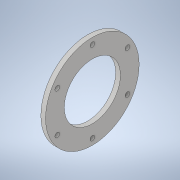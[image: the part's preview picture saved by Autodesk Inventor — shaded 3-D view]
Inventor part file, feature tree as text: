
AUTODESK INVENTOR PART (.ipt)
format: ipt  version: 2021 (Build 250183000, 183)  size: 120,320 bytes
history: native  units: in
note: dims shown in document units (in); Inventor stores cm internally (conversion verified against a paired STEP export)
features: extrude x2, sketch x2
ambient origin geometry x8: Origin, YZ Plane, XZ Plane, XY Plane, X Axis, Y Axis, Z Axis, Center Point
bodies: Solid1 (feature_tree)
feature tree (4):
  extrude  "Extrusion1"  Depth=0.25in
  extrude  "Extrusion2"  Depth=0.25in TaperAngle=360.0deg
  sketch  "Sketch1"  dims[d0=5.0in d1=0.25in]
  sketch  "Sketch2"  dims[d2=2.1655in d3=2.3622in d5=360.0deg d7=0.25in d8=0.0in d9=3.0in d10=0.25in d11=0.0in]
